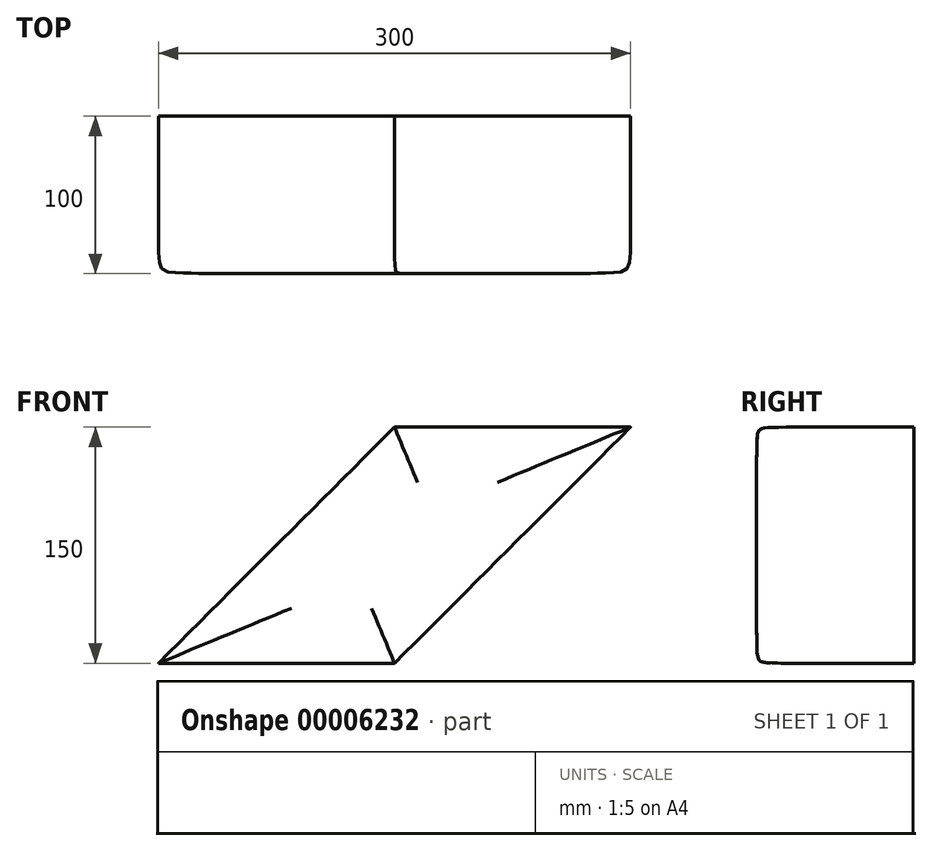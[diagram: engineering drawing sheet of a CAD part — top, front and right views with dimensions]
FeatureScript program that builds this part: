
annotation { "Feature Type Name" : "Feature", "Feature Type Description" : "" }
export const myFeature = defineFeature(function(context is Context, id is Id, definition is map)
    precondition{}
    {
        {
            var Q0;
            Q0=qCreatedBy(makeId("Front.planeOp"),FACE);
            var sketch = newSketch(context, id + "F0", { "sketchPlane" : qUnion([Q0])});
            skLineSegment(sketch, "E0.rect.bottom", {"start": v(75, 75) * mm, "end": v(-75, 75) * mm, "construction": true});
            skLineSegment(sketch, "E0.rect.top", {"start": v(75, -75) * mm, "end": v(-75, -75) * mm, "construction": true});
            skLineSegment(sketch, "E0.rect.left", {"start": v(75, 75) * mm, "end": v(75, -75) * mm, "construction": true});
            skLineSegment(sketch, "E0.rect.right", {"start": v(-75, 75) * mm, "end": v(-75, -75) * mm, "construction": true});
            skPoint(sketch, "E0.rect.middle", {"position": v(0, 0) * mm});
            skLineSegment(sketch, "E1", {"start": v(-75, -75) * mm, "end": v(75, 75) * mm});
            skLineSegment(sketch, "E2", {"start": v(-75, -75) * mm, "end": v(75, -75) * mm});
            skLineSegment(sketch, "E3", {"start": v(75, -75) * mm, "end": v(225, 75) * mm});
            skLineSegment(sketch, "E4", {"start": v(225, 75) * mm, "end": v(75, 75) * mm});
            skSolve(sketch);
        }
        {
            var Q0;
            Q0=makeQuery(id+"F0.imprint","IMPRINT",FACE,{"disambiguationData":[TD([[makeQuery(id+"F0.imprint","IMPRINT",EDGE,{"derivedFrom":sQuery(id+"F0.wireOp",EDGE,"00177815-686a-4fd6-a7d9-c6f9a9fc9b6c")}),-1.0]])]});
            var Q1;
            Q1=makeQuery(id+"F0.imprint","IMPRINT",FACE,{"disambiguationData":[TD([[makeQuery(id+"F0.imprint","IMPRINT",EDGE,{"derivedFrom":sQuery(id+"F0.wireOp",EDGE,"E1")}),-1.0]])]});
            extrude(context, id + "F1", {"entities" : qUnion([Q0, Q1]), "depth" : 100 * mm});
        }
        {
            var Q0;
            Q0=makeQuery(id+"F1.opExtrude","CAP_FACE",FACE,{"disambiguationData":[OSD([sQuery(id+"F0.wireOp",EDGE,"E1"),sQuery(id+"F0.wireOp",EDGE,"E2"),sQuery(id+"F0.wireOp",EDGE,"E3"),sQuery(id+"F0.wireOp",EDGE,"E4")])],"isStart":false});
            fillet(context, id + "F2", {"entities" : qUnion([Q0]), "radius" : 35 * mm, "tangentPropagation" : true, "rho" : 0.9, "crossSection" : FilletCrossSection.CONIC, "allowEdgeOverflow" : false});
        }
    });
